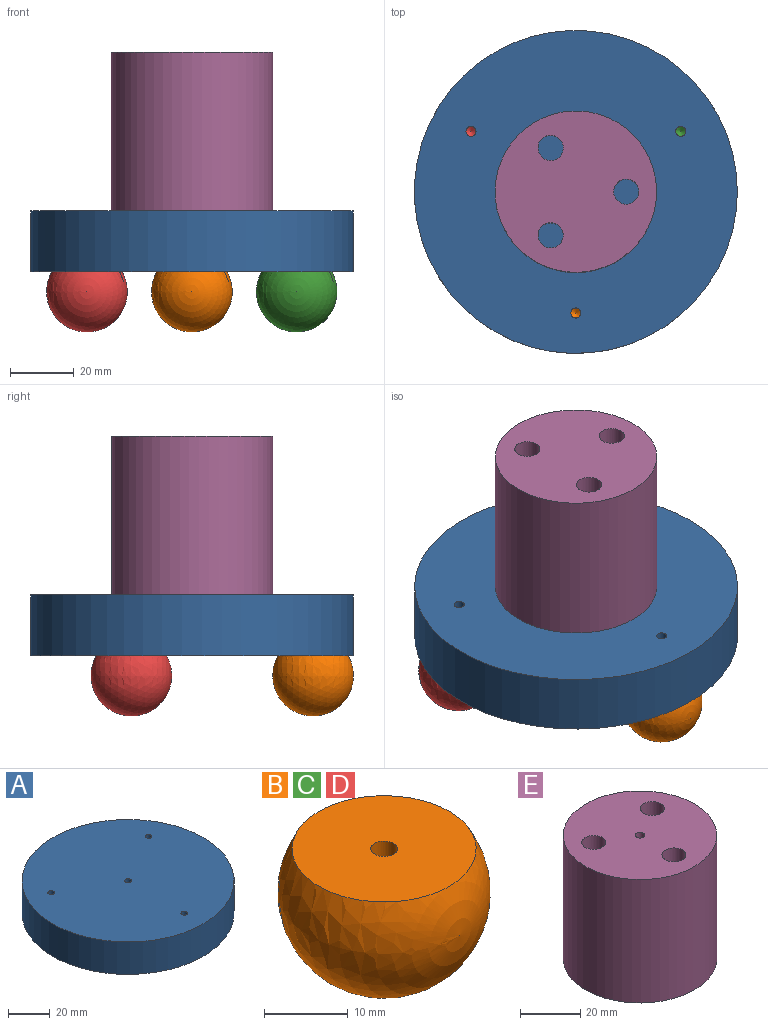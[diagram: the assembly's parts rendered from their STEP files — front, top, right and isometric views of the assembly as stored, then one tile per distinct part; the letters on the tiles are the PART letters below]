
ASSEMBLY  parts=5 mates=8
PART A: 7 faces, bbox 101.6x101.6x19.1 mm
  f0: cylinder r=50.8mm len=101.6mm, axis (0,0,-1), area 6080.5mm2, adj f1,f2
  f1: plane 101.6x101.6mm, normal (0,0,1), area 8075.7mm2, adj f0,f3,f4,f5,f6
  f2: plane 101.6x101.6mm, normal (0,0,-1), area 8075.7mm2, adj f0,f3,f4,f5,f6
  f3: cylinder r=1.59mm len=19.05mm, axis (0,0,1), area 190mm2, adj f1,f2
  f4: cylinder r=1.59mm len=19.05mm, axis (0,0,1), area 190mm2, adj f1,f2
  f5: cylinder r=1.59mm len=19.05mm, axis (0,0,1), area 190mm2, adj f1,f2
  f6: cylinder r=1.59mm len=19.05mm, axis (0,0,1), area 190mm2, adj f1,f2
PART B: 4 faces, bbox 25.4x25.4x25.4 mm
  f0: sphere r=12.7mm, area 1520.1mm2, adj f1
  f1: plane 22x22mm, normal (0,0,1), area 372.1mm2, adj f0,f3
  f2: cone r=0mm half-angle=59deg, axis (0,0,1), area 9.2mm2, adj f3
  f3: cylinder r=1.59mm len=6.35mm, axis (0,0,1), area 63.3mm2, adj f1,f2
PART C: same geometry as B
PART D: same geometry as B
PART E: 8 faces, bbox 50.8x50.8x50 mm
  f0: plane 50.8x50.8mm, normal (0,0,1), area 1870.5mm2, adj f2,f3,f4,f5,f7
  f1: plane 50.8x50.8mm, normal (0,0,-1), area 1878.4mm2, adj f2,f3,f4,f5
  f2: cylinder r=3.97mm len=50mm, axis (0,0,1), area 1246.8mm2, adj f0,f1
  f3: cylinder r=3.97mm len=50mm, axis (0,0,1), area 1246.8mm2, adj f0,f1
  f4: cylinder r=3.97mm len=50mm, axis (0,0,1), area 1246.8mm2, adj f0,f1
  f5: cylinder r=25.4mm len=50.8mm, axis (0,0,1), area 7979.6mm2, adj f0,f1
  f6: cone r=0mm half-angle=59deg, axis (0,0,1), area 9.2mm2, adj f7
  f7: cylinder r=1.59mm len=12.7mm, axis (0,0,1), area 126.7mm2, adj f0,f6
PLACE A at identity
PLACE B t=(0,-38.1,-6.35)mm
PLACE C t=(33,19.05,-6.35)mm
PLACE D t=(-33,19.05,-6.35)mm
PLACE E rot(axis=(-0.71,0.71,0),180deg) t=(0,0,69.05)mm
MATE cylindrical E.f6 <-> A.f0  axis (0,0,-1) through (0,0,19.05)mm
MATE planar B.f2 <-> C.f2  axis (0,0,1) through (0,-38.1,0)mm
MATE cylindrical C.f2 <-> A.f5  axis (0,0,1) through (33,19.05,0)mm
MATE planar A.f0 <-> C.f2  axis (0,0,-1) through (0,0,0)mm
MATE planar D.f2 <-> B.f2  axis (0,0,1) through (-33,19.05,0)mm
MATE cylindrical B.f2 <-> A.f3  axis (0,0,1) through (0,-38.1,0)mm
MATE planar E.f5 <-> A.f0  axis (0,0,-1) through (0,0,19.05)mm
MATE cylindrical D.f2 <-> A.f4  axis (0,0,1) through (-33,19.05,0)mm
